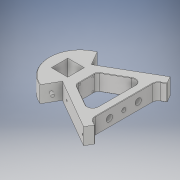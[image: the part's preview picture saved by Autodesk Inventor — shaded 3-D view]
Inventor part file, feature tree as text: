
AUTODESK INVENTOR PART (.ipt)
format: ipt  version: 2019 (Build 230136000, 136)  size: 265,728 bytes
history: native  units: mm
features: sketch x8, extrude x5, fillet x5, hole x3
ambient origin geometry x8: Origin, YZ Plane, XZ Plane, XY Plane, X Axis, Y Axis, Z Axis, Center Point
bodies: Solid1 (feature_tree)
feature tree (21):
  extrude  "Extrusion1"  Depth=40.0mm
  extrude  "Extrusion2"  Depth=20.0mm
  extrude  "Extrusion3"  Depth=40.0mm
  extrude  "Extrusion4"  Depth=40.0mm
  fillet  "Fillet1"  Radius=10.0mm
  fillet  "Fillet2"  Radius=40.0mm
  fillet  "Fillet3"  Radius=40.0mm
  hole  "Hole1"  [1 undecoded]
  hole  "Hole2"  [1 undecoded]
  fillet  "Fillet8"  Radius=25.0mm
  fillet  "Fillet9"  Radius=40.0mm
  sketch  "Sketch8"  dims[d26=10.0mm d27=13.0mm]
  hole  "Hole4"  [1 undecoded]
  extrude  "Extrusion6"  Depth=1.0mm
  sketch  "Sketch1"  dims[d3=40.0mm d4=140.0mm]
  sketch  "Sketch2"  dims[d5=20.0mm d7=20.0mm]
  sketch  "Sketch3"  dims[d8=40.0mm d9=0.0mm d10=6.8mm]
  sketch  "Sketch4"  dims[d11=10.0mm d12=0.0mm d13=6.8mm d14=10.0mm d15=0.0mm d16=40.0mm d17=40.0mm]
  sketch  "Sketch5"  dims[d19=70.0mm d20=75.0mm]
  sketch  "Sketch6"  dims[d21=20.0mm d22=85.0mm d23=25.0mm d24=40.0mm d25=0.0mm]
  sketch  "Sketch9"  dims[d28=15.0mm d29=4.0mm d30=6.0mm d31=5.0mm d32=2.0mm d33=14.3117mm d34=4.0mm d35=0.0mm d36=4.0mm d37=6.0mm d38=5.0mm d39=2.0mm d40=14.3117mm d41=4.0mm d42=0.0mm d47=1.0mm d48=1.0mm d56=15.0mm d57=15.0mm d58=20.0mm d59=35.0mm d60=35.0mm d64=19.0mm d67=15.5mm d68=15.5mm d69=15.5mm d70=15.5mm d71=15.5mm d72=15.5mm d73=15.5mm d74=15.5mm d75=4.0mm d76=50.8mm d77=5.0mm d78=2.0mm d79=90.0deg d80=15.0mm d81=20.594885mm d82=10.0mm d83=20.0mm d84=0.0mm]
note: 3 required parameter values undecoded (feature->parameter linkage not recoverable at this tier; creation-order binding heuristic only, values carry confidence <= 0.55)
